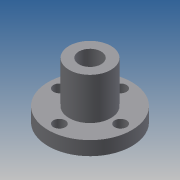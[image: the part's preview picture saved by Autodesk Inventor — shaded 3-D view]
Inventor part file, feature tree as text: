
AUTODESK INVENTOR PART (.ipt)
format: ipt  version: 2013 (Build 170138000, 138)  size: 101,888 bytes
history: native  units: mm
features: extrude x4, sketch x4, pattern_circular x1
ambient origin geometry x8: Origin, YZ Plane, XZ Plane, XY Plane, X Axis, Y Axis, Z Axis, Center Point
bodies: Solid1 (feature_tree)
feature tree (9):
  extrude  "Extrusion1"  Depth=5.0mm TaperAngle=0.0deg
  extrude  "Extrusion2"  Depth=15.0mm TaperAngle=0.0deg
  extrude  "Extrusion3"  Depth=15.0mm TaperAngle=0.0deg
  extrude  "Extrusion4"  Depth=4.3mm
  pattern_circular  "Circular Pattern1"  [2 undecoded]
  sketch  "Sketch1"  dims[d0=30.0mm d2=5.0mm d3=0.0mm]
  sketch  "Sketch2"  dims[d4=15.0mm d6=15.0mm d7=0.0mm]
  sketch  "Sketch3"  dims[d8=8.0mm d11=15.0mm d12=0.0mm]
  sketch  "Sketch4"  dims[d13=11.0mm d14=4.3mm d15=15.0mm d16=0.0mm d17=40.0mm d18=360.0deg]
note: 2 required parameter values undecoded (feature->parameter linkage not recoverable at this tier; creation-order binding heuristic only, values carry confidence <= 0.55)
